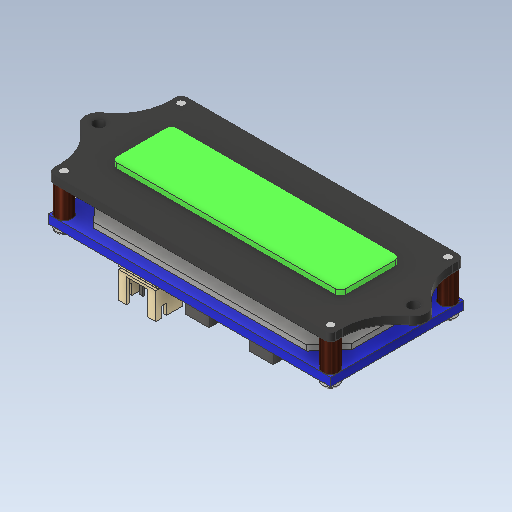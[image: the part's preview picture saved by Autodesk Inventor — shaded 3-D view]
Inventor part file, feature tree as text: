
AUTODESK INVENTOR PART (.ipt)
format: ipt  version: 2020.1 (Build 241239000, 239)  size: 1,615,872 bytes
history: native  units: mm
features: extrude x14, sketch x5, fillet x2, other x2, plane x1, chamfer x1
ambient origin geometry x8: Origin, YZ Plane, XZ Plane, XY Plane, X Axis, Y Axis, Z Axis, Center Point
bodies: Solid1 (feature_tree)
feature tree (25):
  sketch  "Sketch1"  dims[d0=25.0mm d1=53.0mm]
  extrude  "Extrusion1"  Depth=53.0mm
  extrude  "Extrusion2"  Depth=3.0mm
  fillet  "Fillet1"  Radius=2.5mm
  extrude  "Extrusion3"  Depth=43.0mm
  extrude  "Extrusion4"  Depth=1.0mm
  plane  "Work Plane1"
  sketch  "Sketch4"  dims[d40=10.0mm d45=43.0mm]
  extrude  "Extrusion5"  Depth=0.5mm TaperAngle=0.0deg
  extrude  "Extrusion6"  Depth=0.5mm TaperAngle=0.0deg
  extrude  "Extrusion8"  Depth=0.5mm
  fillet  "Fillet3"  Radius=1.5mm
  extrude  "Extrusion12"  Depth=0.5mm
  extrude  "Extrusion7"  Depth=0.5mm
  extrude  "Extrusion14"  Depth=0.5mm TaperAngle=0.0deg
  extrude  "Extrusion15"  Depth=0.5mm
  extrude  "Extrusion16"  Depth=0.5mm
  extrude  "Extrusion17"  Depth=0.5mm
  chamfer  "Chamfer2"  Distance=3.0mm
  extrude  "Extrusion18"  Depth=0.5mm TaperAngle=0.0deg
  other  "Image1"
  sketch  "Sketch3"  dims[d29=2.1mm d37=3.0mm d38=2.5mm]
  other  "Image2"
  sketch  "Sketch6"  dims[d46=11.3mm d47=1.0mm]
  sketch  "Sketch7"  dims[d48=1.0mm d60=1.5mm d61=0.0mm d62=1.0mm d63=0.0mm d64=1.0mm d65=1.5mm d69=1.5mm d70=1.5mm d73=0.1mm d74=0.0mm d75=3.0mm d76=3.0mm d77=3.0mm d78=3.0mm d79=8.03mm d80=0.0mm d81=-1.0mm d83=1.57mm d84=0.0mm d98=7.0mm d99=4.5mm d100=4.5mm d101=4.5mm d104=11.0mm d105=7.5mm d106=5.0mm d107=5.5mm d114=0.0mm d115=0.0mm d125=2.5mm d127=2.25mm d128=2.25mm d129=2.5mm d130=2.25mm d131=2.25mm d133=2.0mm d134=0.0mm d135=1.0mm d136=0.0mm d138=3.0mm d139=0.0mm d151=0.5mm d157=0.2mm d158=0.2mm d161=0.2mm d162=20.0mm d163=2.0mm d164=2.5mm d165=6.0mm d166=1.0mm d167=0.0mm d171=0.5mm d173=1.0mm d174=1.0mm d175=0.5mm d176=0.5mm d177=0.3mm d179=1.48mm d180=4.0mm d183=6.0mm d184=0.0mm d185=4.0mm d186=0.0mm d187=1.5mm d188=0.0mm d189=5.0mm d190=0.0mm d191=0.2mm d192=2.0mm d193=45.0deg d194=0.5mm d195=0.5mm d196=1.0mm d197=5.0mm d198=0.0mm]
